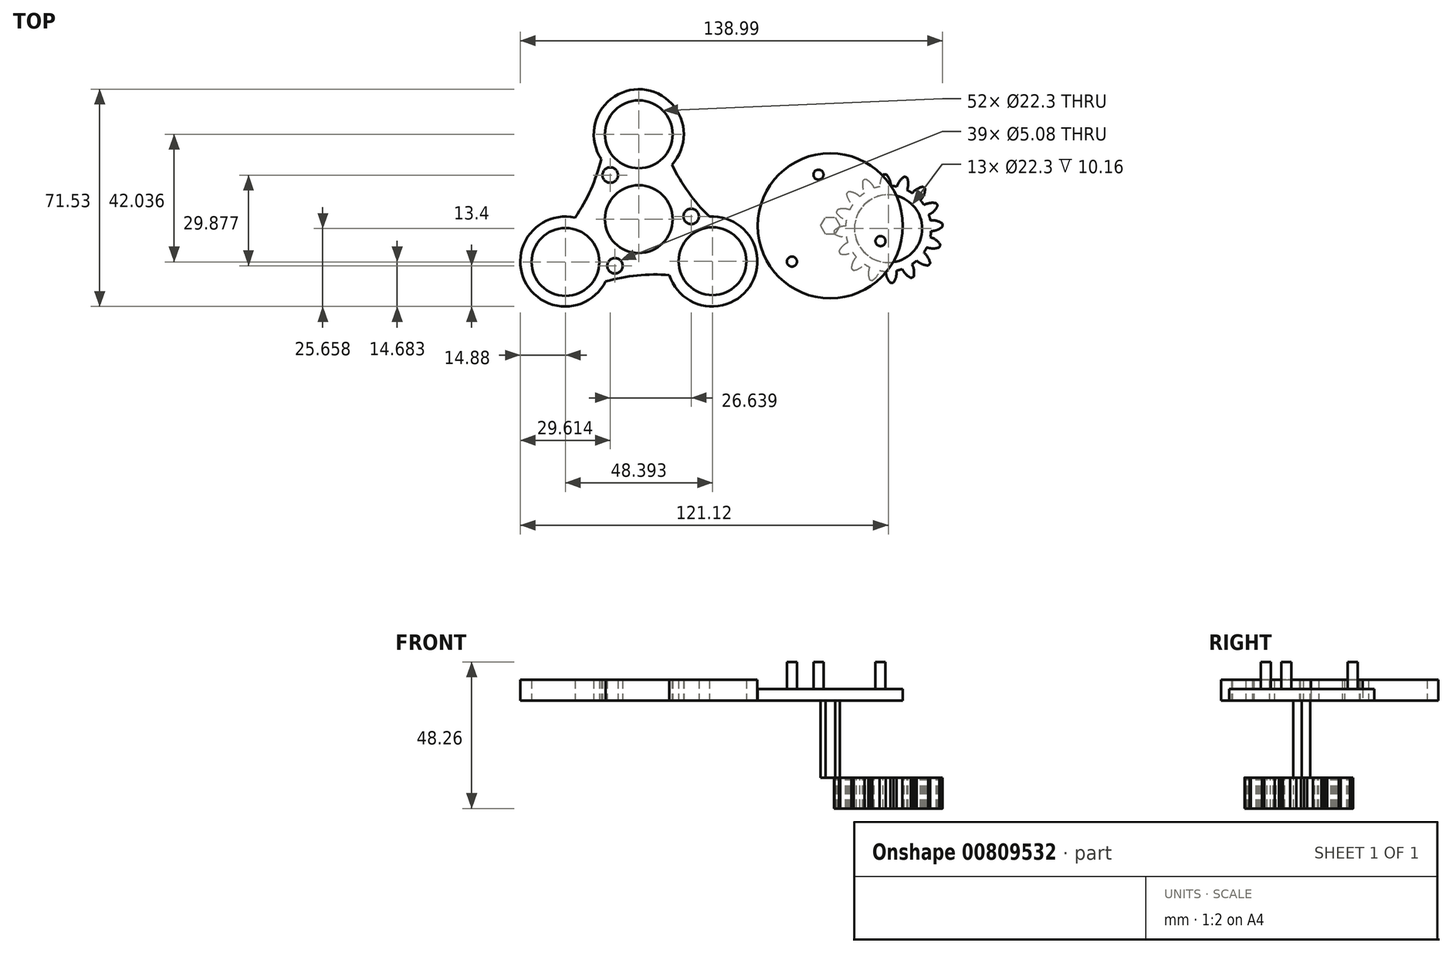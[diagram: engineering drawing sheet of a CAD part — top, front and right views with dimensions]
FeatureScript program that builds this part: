
annotation { "Feature Type Name" : "Feature", "Feature Type Description" : "" }
export const myFeature = defineFeature(function(context is Context, id is Id, definition is map)
    precondition{}
    {
        {
            var Q0;
            Q0=qCreatedBy(makeId("Top.planeOp"),FACE);
            var sketch = newSketch(context, id + "F0", { "sketchPlane" : qUnion([Q0])});
            skCircle(sketch, "E0.2.0", {"center": v(-27.04, 2.27) * mm, "radius": 11.15 * mm});
            skCircle(sketch, "E1.2.0", {"center": v(-27.04, 30.2) * mm, "radius": 11.15 * mm});
            skCircle(sketch, "E2", {"center": v(-27.04, 2.27) * mm, "radius": 43.18 * mm, "construction": true});
            skCircle(sketch, "E3.1.0", {"center": v(-51.16, -11.83) * mm, "radius": 11.15 * mm});
            skCircle(sketch, "E3.2.0", {"center": v(-2.77, -11.57) * mm, "radius": 11.15 * mm});
            skArc(sketch, "E4", {"start": v(-48.02, 2.75) * mm, "mid": v(-42.84, 12) * mm, "end": v(-39.36, 22) * mm});
            skArc(sketch, "E5.1.0", {"start": v(-16.96, -16.14) * mm, "mid": v(-27.56, -16.28) * mm, "end": v(-37.96, -18.26) * mm});
            skArc(sketch, "E5.2.0", {"start": v(-17.24, 22.65) * mm, "mid": v(-17.21, 22.59) * mm, "end": v(-17.18, 22.53) * mm});
            skCircle(sketch, "E6", {"center": v(-36.43, 16.77) * mm, "radius": 2.54 * mm});
            skCircle(sketch, "E7.1.0", {"center": v(-34.9, -13.11) * mm, "radius": 2.54 * mm});
            skCircle(sketch, "E7.2.0", {"center": v(-9.79, 3.15) * mm, "radius": 2.54 * mm});
            skArc(sketch, "E8", {"start": v(-16.13, 20.2) * mm, "mid": v(-25.9, 44.97) * mm, "end": v(-39.36, 22) * mm});
            skArc(sketch, "E9.trimOffspring", {"start": v(-16.13, 20.2) * mm, "mid": v(-10.71, 11.1) * mm, "end": v(-3.8, 3.07) * mm});
            skArc(sketch, "E10.1.0", {"start": v(-48.02, 2.75) * mm, "mid": v(-64.59, -18.1) * mm, "end": v(-37.96, -18.26) * mm});
            skArc(sketch, "E10.2.0", {"start": v(-16.96, -16.14) * mm, "mid": v(9.37, -20.07) * mm, "end": v(-3.8, 3.07) * mm});
            skSolve(sketch);
        }
        {
            var Q0;
            Q0=qCreatedBy(makeId("Top.planeOp"),FACE);
            var sketch = newSketch(context, id + "F1", { "sketchPlane" : qUnion([Q0])});
            skCircle(sketch, "E11", {"center": v(32.1, 16.9) * mm, "radius": 1.65 * mm});
            skCircle(sketch, "E12.1.0", {"center": v(23.36, -11.7) * mm, "radius": 1.65 * mm});
            skCircle(sketch, "E12.2.0", {"center": v(52.5, -4.97) * mm, "radius": 1.65 * mm});
            skPoint(sketch, "E12.center", {"position": v(36, 0.08) * mm});
            skCircle(sketch, "E13", {"center": v(36, 0.08) * mm, "radius": 23.88 * mm});
            skPoint(sketch, "E14.0.midPoint", {"position": v(45.07, -11.58) * mm});
            skPoint(sketch, "E15.orphan", {"position": v(38.31, -5.6) * mm});
            skPoint(sketch, "E16.orphan", {"position": v(51.83, -17.56) * mm});
            skCircle(sketch, "E17.cCircle", {"center": v(36, 0.08) * mm, "radius": 2.75 * mm, "construction": true});
            skLineSegment(sketch, "E17.0", {"start": v(37.58, -2.67) * mm, "end": v(34.4, -2.67) * mm});
            skLineSegment(sketch, "E17.1", {"start": v(34.4, -2.67) * mm, "end": v(32.82, 0.08) * mm});
            skLineSegment(sketch, "E17.2", {"start": v(32.82, 0.08) * mm, "end": v(34.4, 2.83) * mm});
            skLineSegment(sketch, "E17.3", {"start": v(34.4, 2.83) * mm, "end": v(37.58, 2.83) * mm});
            skLineSegment(sketch, "E17.4", {"start": v(37.58, 2.83) * mm, "end": v(39.17, 0.08) * mm});
            skLineSegment(sketch, "E17.5", {"start": v(39.17, 0.08) * mm, "end": v(37.58, -2.67) * mm});
            skPoint(sketch, "E17.0.midPoint", {"position": v(36, -2.67) * mm});
            skSolve(sketch);
        }
        {
            var Q0;
            Q0=qCreatedBy(makeId("Top.planeOp"),FACE);
            cPlane(context, id + "F2", {"entities" : qUnion([Q0]), "cplaneType" : CPlaneType.OFFSET, "offset" : 25.4 * mm, "oppositeDirection" : true, "width" : 152.4 * mm, "height" : 152.4 * mm});
        }
        {
            var Q0;
            Q0=qCreatedBy(id+"F2.planeOp",FACE);
            var sketch = newSketch(context, id + "F3", { "sketchPlane" : qUnion([Q0])});
            skCircle(sketch, "E18", {"center": v(55.08, -0.85) * mm, "radius": 11.15 * mm});
            skPoint(sketch, "E19.center", {"position": v(53.8, -0.6) * mm});
            skPoint(sketch, "E20.center", {"position": v(55.03, 0.18) * mm});
            skArc(sketch, "E21", {"start": v(47.3, 10.9) * mm, "mid": v(46.49, 10.33) * mm, "end": v(45.72, 9.7) * mm});
            skArc(sketch, "E22", {"start": v(55.53, 15.17) * mm, "mid": v(55.05, 16.14) * mm, "end": v(54.4, 17) * mm});
            skArc(sketch, "E23", {"start": v(55.92, 13.21) * mm, "mid": v(55.81, 14.2) * mm, "end": v(55.53, 15.17) * mm});
            skArc(sketch, "E24.MirrorCS", {"start": v(52.52, 14.97) * mm, "mid": v(52.87, 16) * mm, "end": v(53.41, 16.94) * mm});
            skArc(sketch, "E25.MirrorCS", {"start": v(52.4, 12.98) * mm, "mid": v(52.37, 13.98) * mm, "end": v(52.52, 14.97) * mm});
            skArc(sketch, "E26", {"start": v(54.4, 17) * mm, "mid": v(53.9, 17.02) * mm, "end": v(53.41, 16.94) * mm});
            skCircle(sketch, "E27", {"center": v(55.03, 0.18) * mm, "radius": 43.18 * mm, "construction": true});
            skArc(sketch, "E28.1.0", {"start": v(46.66, 12.78) * mm, "mid": v(46.6, 13.87) * mm, "end": v(46.73, 14.95) * mm});
            skArc(sketch, "E28.1.1", {"start": v(47.6, 15.38) * mm, "mid": v(47.15, 15.2) * mm, "end": v(46.73, 14.95) * mm});
            skArc(sketch, "E28.1.2", {"start": v(49.37, 14.12) * mm, "mid": v(48.55, 14.84) * mm, "end": v(47.6, 15.38) * mm});
            skArc(sketch, "E28.1.3", {"start": v(50.47, 12.46) * mm, "mid": v(50, 13.34) * mm, "end": v(49.37, 14.12) * mm});
            skArc(sketch, "E28.1.4", {"start": v(47.3, 10.9) * mm, "mid": v(46.9, 11.81) * mm, "end": v(46.66, 12.78) * mm});
            skArc(sketch, "E28.2.0", {"start": v(42.08, 8.52) * mm, "mid": v(41.6, 9.5) * mm, "end": v(41.32, 10.55) * mm});
            skArc(sketch, "E28.2.1", {"start": v(41.97, 11.29) * mm, "mid": v(41.6, 10.95) * mm, "end": v(41.32, 10.55) * mm});
            skArc(sketch, "E28.2.2", {"start": v(44.07, 10.8) * mm, "mid": v(43.04, 11.14) * mm, "end": v(41.97, 11.29) * mm});
            skArc(sketch, "E28.2.3", {"start": v(45.73, 9.69) * mm, "mid": v(44.95, 10.31) * mm, "end": v(44.07, 10.8) * mm});
            skArc(sketch, "E28.2.4", {"start": v(43.4, 7.03) * mm, "mid": v(42.67, 7.72) * mm, "end": v(42.08, 8.52) * mm});
            skArc(sketch, "E28.3.0", {"start": v(39.48, 2.83) * mm, "mid": v(38.67, 3.55) * mm, "end": v(38, 4.42) * mm});
            skArc(sketch, "E28.3.1", {"start": v(38.32, 5.35) * mm, "mid": v(38.12, 4.9) * mm, "end": v(38, 4.42) * mm});
            skArc(sketch, "E28.3.2", {"start": v(40.45, 5.7) * mm, "mid": v(39.37, 5.62) * mm, "end": v(38.32, 5.35) * mm});
            skArc(sketch, "E28.3.3", {"start": v(42.4, 5.3) * mm, "mid": v(41.45, 5.59) * mm, "end": v(40.45, 5.7) * mm});
            skArc(sketch, "E28.3.4", {"start": v(41.27, 1.96) * mm, "mid": v(40.34, 2.32) * mm, "end": v(39.48, 2.83) * mm});
            skArc(sketch, "E28.4.0", {"start": v(39.26, -3.42) * mm, "mid": v(38.23, -3.06) * mm, "end": v(37.29, -2.52) * mm});
            skArc(sketch, "E28.4.1", {"start": v(37.22, -1.54) * mm, "mid": v(37.21, -2.03) * mm, "end": v(37.29, -2.52) * mm});
            skArc(sketch, "E28.4.2", {"start": v(39.06, -0.4) * mm, "mid": v(38.09, -0.88) * mm, "end": v(37.22, -1.54) * mm});
            skArc(sketch, "E28.4.3", {"start": v(41.01, -0.01) * mm, "mid": v(40.02, -0.12) * mm, "end": v(39.06, -0.4) * mm});
            skArc(sketch, "E28.4.4", {"start": v(41.24, -3.54) * mm, "mid": v(40.25, -3.56) * mm, "end": v(39.26, -3.42) * mm});
            skArc(sketch, "E28.5.0", {"start": v(41.45, -9.27) * mm, "mid": v(40.36, -9.34) * mm, "end": v(39.28, -9.2) * mm});
            skArc(sketch, "E28.5.1", {"start": v(38.84, -8.32) * mm, "mid": v(39.02, -8.78) * mm, "end": v(39.28, -9.2) * mm});
            skArc(sketch, "E28.5.2", {"start": v(40.1, -6.56) * mm, "mid": v(39.4, -7.38) * mm, "end": v(38.84, -8.32) * mm});
            skArc(sketch, "E28.5.3", {"start": v(41.76, -5.46) * mm, "mid": v(40.89, -5.94) * mm, "end": v(40.1, -6.56) * mm});
            skArc(sketch, "E28.5.4", {"start": v(43.33, -8.63) * mm, "mid": v(42.41, -9.03) * mm, "end": v(41.45, -9.27) * mm});
            skArc(sketch, "E28.6.0", {"start": v(45.7, -13.85) * mm, "mid": v(44.73, -14.33) * mm, "end": v(43.68, -14.61) * mm});
            skArc(sketch, "E28.6.1", {"start": v(42.94, -13.97) * mm, "mid": v(43.28, -14.32) * mm, "end": v(43.68, -14.61) * mm});
            skArc(sketch, "E28.6.2", {"start": v(43.43, -11.86) * mm, "mid": v(43.08, -12.89) * mm, "end": v(42.94, -13.97) * mm});
            skArc(sketch, "E28.6.3", {"start": v(44.54, -10.2) * mm, "mid": v(43.91, -10.98) * mm, "end": v(43.43, -11.86) * mm});
            skArc(sketch, "E28.6.4", {"start": v(47.2, -12.54) * mm, "mid": v(46.5, -13.26) * mm, "end": v(45.7, -13.85) * mm});
            skArc(sketch, "E28.7.0", {"start": v(51.4, -16.45) * mm, "mid": v(50.67, -17.26) * mm, "end": v(49.81, -17.93) * mm});
            skArc(sketch, "E28.7.1", {"start": v(48.88, -17.61) * mm, "mid": v(49.33, -17.81) * mm, "end": v(49.81, -17.93) * mm});
            skArc(sketch, "E28.7.2", {"start": v(48.53, -15.48) * mm, "mid": v(48.6, -16.56) * mm, "end": v(48.88, -17.61) * mm});
            skArc(sketch, "E28.7.3", {"start": v(48.92, -13.53) * mm, "mid": v(48.64, -14.49) * mm, "end": v(48.53, -15.48) * mm});
            skArc(sketch, "E28.7.4", {"start": v(52.27, -14.66) * mm, "mid": v(51.9, -15.6) * mm, "end": v(51.4, -16.45) * mm});
            skArc(sketch, "E28.8.0", {"start": v(57.64, -16.67) * mm, "mid": v(57.29, -17.7) * mm, "end": v(56.75, -18.65) * mm});
            skArc(sketch, "E28.8.1", {"start": v(55.77, -18.71) * mm, "mid": v(56.26, -18.72) * mm, "end": v(56.75, -18.65) * mm});
            skArc(sketch, "E28.8.2", {"start": v(54.63, -16.87) * mm, "mid": v(55.1, -17.85) * mm, "end": v(55.77, -18.71) * mm});
            skArc(sketch, "E28.8.3", {"start": v(54.24, -14.92) * mm, "mid": v(54.35, -15.91) * mm, "end": v(54.63, -16.87) * mm});
            skArc(sketch, "E28.8.4", {"start": v(57.77, -14.69) * mm, "mid": v(57.8, -15.69) * mm, "end": v(57.64, -16.67) * mm});
            skArc(sketch, "E28.9.0", {"start": v(63.5, -14.49) * mm, "mid": v(63.57, -15.57) * mm, "end": v(63.43, -16.65) * mm});
            skArc(sketch, "E28.9.1", {"start": v(62.55, -17.09) * mm, "mid": v(63, -16.9) * mm, "end": v(63.43, -16.65) * mm});
            skArc(sketch, "E28.9.2", {"start": v(60.8, -15.83) * mm, "mid": v(61.61, -16.54) * mm, "end": v(62.55, -17.09) * mm});
            skArc(sketch, "E28.9.3", {"start": v(59.69, -14.17) * mm, "mid": v(60.17, -15.05) * mm, "end": v(60.8, -15.83) * mm});
            skArc(sketch, "E28.9.4", {"start": v(62.86, -12.6) * mm, "mid": v(63.26, -13.52) * mm, "end": v(63.5, -14.49) * mm});
            skArc(sketch, "E28.10.0", {"start": v(68.08, -10.23) * mm, "mid": v(68.56, -11.2) * mm, "end": v(68.84, -12.26) * mm});
            skArc(sketch, "E28.10.1", {"start": v(68.2, -13) * mm, "mid": v(68.55, -12.65) * mm, "end": v(68.84, -12.26) * mm});
            skArc(sketch, "E28.10.2", {"start": v(66.09, -12.5) * mm, "mid": v(67.12, -12.85) * mm, "end": v(68.2, -13) * mm});
            skArc(sketch, "E28.10.3", {"start": v(64.43, -11.4) * mm, "mid": v(65.21, -12.02) * mm, "end": v(66.09, -12.5) * mm});
            skArc(sketch, "E28.10.4", {"start": v(66.76, -8.74) * mm, "mid": v(67.49, -9.42) * mm, "end": v(68.08, -10.23) * mm});
            skArc(sketch, "E28.11.0", {"start": v(70.68, -4.54) * mm, "mid": v(71.5, -5.26) * mm, "end": v(72.16, -6.12) * mm});
            skArc(sketch, "E28.11.1", {"start": v(71.84, -7.05) * mm, "mid": v(72.04, -6.6) * mm, "end": v(72.16, -6.12) * mm});
            skArc(sketch, "E28.11.2", {"start": v(69.7, -7.4) * mm, "mid": v(70.8, -7.33) * mm, "end": v(71.84, -7.05) * mm});
            skArc(sketch, "E28.11.3", {"start": v(67.75, -7.01) * mm, "mid": v(68.71, -7.3) * mm, "end": v(69.7, -7.4) * mm});
            skArc(sketch, "E28.11.4", {"start": v(68.9, -3.66) * mm, "mid": v(69.82, -4.02) * mm, "end": v(70.68, -4.54) * mm});
            skArc(sketch, "E28.12.0", {"start": v(70.9, 1.71) * mm, "mid": v(71.93, 1.36) * mm, "end": v(72.87, 0.81) * mm});
            skArc(sketch, "E28.12.1", {"start": v(72.94, -0.16) * mm, "mid": v(72.95, 0.33) * mm, "end": v(72.87, 0.81) * mm});
            skArc(sketch, "E28.12.2", {"start": v(71.1, -1.3) * mm, "mid": v(72.07, -0.82) * mm, "end": v(72.94, -0.16) * mm});
            skArc(sketch, "E28.12.3", {"start": v(69.15, -1.7) * mm, "mid": v(70.14, -1.58) * mm, "end": v(71.1, -1.3) * mm});
            skArc(sketch, "E28.12.4", {"start": v(68.92, 1.83) * mm, "mid": v(69.91, 1.86) * mm, "end": v(70.9, 1.71) * mm});
            skArc(sketch, "E28.13.0", {"start": v(68.71, 7.57) * mm, "mid": v(69.8, 7.64) * mm, "end": v(70.88, 7.5) * mm});
            skArc(sketch, "E28.13.1", {"start": v(71.31, 6.62) * mm, "mid": v(71.14, 7.08) * mm, "end": v(70.88, 7.5) * mm});
            skArc(sketch, "E28.13.2", {"start": v(70.05, 4.86) * mm, "mid": v(70.77, 5.68) * mm, "end": v(71.31, 6.62) * mm});
            skArc(sketch, "E28.13.3", {"start": v(68.4, 3.76) * mm, "mid": v(69.27, 4.24) * mm, "end": v(70.05, 4.86) * mm});
            skArc(sketch, "E28.13.4", {"start": v(66.83, 6.92) * mm, "mid": v(67.75, 7.33) * mm, "end": v(68.71, 7.57) * mm});
            skArc(sketch, "E28.14.0", {"start": v(64.45, 12.15) * mm, "mid": v(65.43, 12.62) * mm, "end": v(66.48, 12.9) * mm});
            skArc(sketch, "E28.14.1", {"start": v(67.22, 12.26) * mm, "mid": v(66.88, 12.62) * mm, "end": v(66.48, 12.9) * mm});
            skArc(sketch, "E28.14.2", {"start": v(66.73, 10.15) * mm, "mid": v(67.07, 11.18) * mm, "end": v(67.22, 12.26) * mm});
            skArc(sketch, "E28.14.3", {"start": v(65.62, 8.5) * mm, "mid": v(66.25, 9.28) * mm, "end": v(66.73, 10.15) * mm});
            skArc(sketch, "E28.14.4", {"start": v(62.96, 10.83) * mm, "mid": v(63.65, 11.55) * mm, "end": v(64.45, 12.15) * mm});
            skArc(sketch, "E28.15.0", {"start": v(58.77, 14.74) * mm, "mid": v(59.49, 15.56) * mm, "end": v(60.35, 16.23) * mm});
            skArc(sketch, "E28.15.1", {"start": v(61.28, 15.9) * mm, "mid": v(60.83, 16.1) * mm, "end": v(60.35, 16.23) * mm});
            skArc(sketch, "E28.15.2", {"start": v(61.63, 13.77) * mm, "mid": v(61.56, 14.86) * mm, "end": v(61.28, 15.9) * mm});
            skArc(sketch, "E28.15.3", {"start": v(61.24, 11.82) * mm, "mid": v(61.52, 12.78) * mm, "end": v(61.63, 13.77) * mm});
            skArc(sketch, "E28.15.4", {"start": v(57.9, 12.96) * mm, "mid": v(58.25, 13.89) * mm, "end": v(58.77, 14.74) * mm});
            skArc(sketch, "E29.trimOffspring", {"start": v(43.4, 7.03) * mm, "mid": v(42.86, 6.19) * mm, "end": v(42.4, 5.3) * mm});
            skArc(sketch, "E30.trimOffspring", {"start": v(41.26, 1.96) * mm, "mid": v(41.1, 0.98) * mm, "end": v(41, -0.01) * mm});
            skArc(sketch, "E31.trimOffspring", {"start": v(41.24, -3.54) * mm, "mid": v(41.46, -4.51) * mm, "end": v(41.75, -5.46) * mm});
            skArc(sketch, "E32.trimOffspring", {"start": v(43.32, -8.63) * mm, "mid": v(43.9, -9.44) * mm, "end": v(44.53, -10.21) * mm});
            skArc(sketch, "E33.trimOffspring", {"start": v(47.2, -12.54) * mm, "mid": v(48.04, -13.07) * mm, "end": v(48.92, -13.53) * mm});
            skArc(sketch, "E34.trimOffspring", {"start": v(52.27, -14.67) * mm, "mid": v(53.25, -14.83) * mm, "end": v(54.24, -14.93) * mm});
            skArc(sketch, "E35.trimOffspring", {"start": v(57.77, -14.7) * mm, "mid": v(58.74, -14.47) * mm, "end": v(59.7, -14.18) * mm});
            skArc(sketch, "E36.trimOffspring", {"start": v(62.86, -12.61) * mm, "mid": v(63.67, -12.03) * mm, "end": v(64.44, -11.4) * mm});
            skArc(sketch, "E37.trimOffspring", {"start": v(66.77, -8.74) * mm, "mid": v(67.3, -7.9) * mm, "end": v(67.76, -7.01) * mm});
            skArc(sketch, "E38.trimOffspring", {"start": v(68.9, -3.67) * mm, "mid": v(69.06, -2.68) * mm, "end": v(69.15, -1.7) * mm});
            skArc(sketch, "E39.trimOffspring", {"start": v(68.92, 1.84) * mm, "mid": v(68.7, 2.8) * mm, "end": v(68.4, 3.76) * mm});
            skArc(sketch, "E40.trimOffspring", {"start": v(66.84, 6.93) * mm, "mid": v(66.26, 7.74) * mm, "end": v(65.63, 8.5) * mm});
            skArc(sketch, "E41.trimOffspring", {"start": v(62.97, 10.84) * mm, "mid": v(62.12, 11.36) * mm, "end": v(61.24, 11.83) * mm});
            skArc(sketch, "E42.trimOffspring", {"start": v(57.9, 12.96) * mm, "mid": v(56.91, 13.13) * mm, "end": v(55.92, 13.22) * mm});
            skArc(sketch, "E43.trimOffspring", {"start": v(52.4, 12.99) * mm, "mid": v(51.42, 12.76) * mm, "end": v(50.47, 12.47) * mm});
            skSolve(sketch);
        }
        {
            var Q0;
            Q0=makeQuery(id+"F3.imprint","IMPRINT",FACE,{"disambiguationData":[TD([[makeQuery(id+"F3.imprint","IMPRINT",EDGE,{"derivedFrom":sQuery(id+"F3.wireOp",EDGE,"E18")}),-1.0]])]});
            extrude(context, id + "F4", {"entities" : qUnion([Q0]), "oppositeDirection" : true, "depth" : 10.16 * mm, "offsetDistance" : 25.4 * mm});
        }
        {
            var Q0;
            Q0=makeQuery(id+"F0.imprint","IMPRINT",FACE,{"disambiguationData":[TD([[makeQuery(id+"F0.imprint","IMPRINT",EDGE,{"derivedFrom":sQuery(id+"F0.wireOp",EDGE,"E0.2.1")}),-1.0]])]});
            var Q1;
            Q1=makeQuery(id+"F0.imprint","IMPRINT",FACE,{"disambiguationData":[TD([[makeQuery(id+"F0.imprint","IMPRINT",EDGE,{"derivedFrom":sQuery(id+"F0.wireOp",EDGE,"E0.2.0")}),-1.0]])]});
            var Q2;
            Q2=makeQuery(id+"F0.imprint","IMPRINT",FACE,{"disambiguationData":[TD([[makeQuery(id+"F0.imprint","IMPRINT",EDGE,{"derivedFrom":sQuery(id+"F0.wireOp",EDGE,"E3.1.0")}),-1.0]])]});
            var Q3;
            Q3=makeQuery(id+"F0.imprint","IMPRINT",FACE,{"disambiguationData":[TD([[makeQuery(id+"F0.imprint","IMPRINT",EDGE,{"derivedFrom":sQuery(id+"F0.wireOp",EDGE,"E3.2.0")}),-1.0]])]});
            var Q4;
            Q4=makeQuery(id+"F0.imprint","IMPRINT",FACE,{"disambiguationData":[TD([[makeQuery(id+"F0.imprint","IMPRINT",EDGE,{"derivedFrom":sQuery(id+"F0.wireOp",EDGE,"E1.2.0")}),-1.0]])]});
            extrude(context, id + "F5", {"entities" : qUnion([Q0, Q1, Q2, Q3, Q4]), "depth" : 6.86 * mm, "offsetDistance" : 25.4 * mm});
        }
        {
            var Q0;
            Q0=makeQuery(id+"F1.imprint","IMPRINT",FACE,{"disambiguationData":[TD([[makeQuery(id+"F1.imprint","IMPRINT",EDGE,{"derivedFrom":sQuery(id+"F1.wireOp",EDGE,"E11")}),-1.0]])]});
            var Q1;
            Q1=makeQuery(id+"F1.imprint","IMPRINT",FACE,{"disambiguationData":[TD([[makeQuery(id+"F1.imprint","IMPRINT",EDGE,{"derivedFrom":sQuery(id+"F1.wireOp",EDGE,"E17.0")}),-1.0]])]});
            extrude(context, id + "F6", {"entities" : qUnion([Q0, Q1]), "depth" : 3.8 * mm, "offsetDistance" : 25.4 * mm});
        }
        {
            var Q0;
            Q0=makeQuery(id+"F1.imprint","IMPRINT",FACE,{"disambiguationData":[TD([[makeQuery(id+"F1.imprint","IMPRINT",EDGE,{"derivedFrom":sQuery(id+"F1.wireOp",EDGE,"E11")}),1.0]])]});
            var Q1;
            Q1=makeQuery(id+"F1.imprint","IMPRINT",FACE,{"disambiguationData":[TD([[makeQuery(id+"F1.imprint","IMPRINT",EDGE,{"derivedFrom":sQuery(id+"F1.wireOp",EDGE,"E12.1.0")}),1.0]])]});
            var Q2;
            Q2=makeQuery(id+"F1.imprint","IMPRINT",FACE,{"disambiguationData":[TD([[makeQuery(id+"F1.imprint","IMPRINT",EDGE,{"derivedFrom":sQuery(id+"F1.wireOp",EDGE,"E12.2.0")}),1.0]])]});
            extrude(context, id + "F7", {"entities" : qUnion([Q0, Q1, Q2]), "operationType" : NewBodyOperationType.ADD, "depth" : 12.7 * mm, "offsetDistance" : 25.4 * mm});
        }
        {
            var Q0;
            Q0=makeQuery(id+"F1.imprint","IMPRINT",FACE,{"disambiguationData":[TD([[makeQuery(id+"F1.imprint","IMPRINT",EDGE,{"derivedFrom":sQuery(id+"F1.wireOp",EDGE,"E17.0")}),-1.0]])]});
            extrude(context, id + "F8", {"entities" : qUnion([Q0]), "oppositeDirection" : true, "depth" : 25.4 * mm, "offsetDistance" : 25.4 * mm});
        }
    });
